# Revit family: VIESSMANN - Vitocell 100-V (CVW.CVWA) 390-500 L
name_source: partatom
category: Wyposażenie mechaniczne
revit_build: Autodesk Revit 2017 (Build: 20160720_1515(x64)
units: mm (PartAtom-declared; Revit-internal decimal feet)

## family parameters
Numer OmniClass = 23.65.35.11.11
Oparty na płaszczyźnie roboczej = Nie
Punkt obliczania pomieszczeń = Nie
Tnij formami wycięć po wczytaniu = Tak
Typ części = Normalny
Tytuł OmniClass = Storage Water Heaters
Współdzielony = Nie
Wymiar okrągłego złącza = Użyj średnicy
Zawsze pionowo = Tak

## types (2) — shared parameters
Autor = https://www.archispace.pl
Ciepła woda użytkowa = 1"
Cyrkulacja = 3/4"
Grzałka elektryczna = 1 1/2"
Klasa efektywności energetycznej = B
Maks. powierzchnia czynna absorbera możliwa do podłączenia do zestawu solarnych wymienników ciepła - Vitosol-F = 11.5 m²
Maks. powierzchnia czynna absorbera możliwa do podłączenia do zestawu solarnych wymienników ciepła - Vitosol-T = 6.0 m²
Numer identyfikacyjny produktu = 9W173-13MC/E
Opis = Podgrzewacz pojemnościowy
Opis indeksowy = 9W173-13MC/E
Podział = 859 mm  [stored 2.81824 ft]
Powrót wody grzewczej = 1 1/4"
Producent = Viessmann Sp.z.o.o.
Przepływ objętościowy wody grzewczej (dla podanych wydajności stałych) = 3.00 m³/h
Przepływ po stronie wody grzewczej = 3.00 m³/h
Szerokość - bez izolacji cieplnej = 881 mm  [stored 2.89042 ft]
Szerokość - z izolacją cieplną = 923 mm  [stored 3.02822 ft]
Szerokość z izolacją cieplną = 923 mm  [stored 3.02822 ft]
URL = https://www.viessmann-projektant.pl
Viessmann Kolor 1 = Viessmann Kolor 1
Viessmann Kolor 2 = Viessmann Kolor 2
Viessmann Kolor 3 = Viessmann Kolor 3
Wysokość króćca cwu z zestawu solarnych wymienników ciepła = 572 mm  [stored 1.87664 ft]
Wysokość króćca powrotu wody grzewczej = 330 mm  [stored 1.08268 ft]
Wysokość króćca zimnej wody użytkowej = 88 mm  [stored 0.288714 ft]
Zasilanie wody grzewczej = 1 1/4"
Zestaw solarnych wymienników ciepła = 3/4"
Zimna woda użytkowa = 1"
Średnica - bez izolacji cieplnej = 650 mm  [stored 2.13255 ft]
Średnica - z izolacją cieplną = 859 mm  [stored 2.81824 ft]
Średnica z izolacją cieplną = 859 mm  [stored 2.81824 ft]

## per-type parameters (varying)
- Zbiornik CVWA 500L: Czas podgrzewu cwu przy podłączonej pompie ciepła o znamionowej mocy cieplnej 16kW i temp. wody na zasilaniu wodą grzewczą wynoszącej 55 lub 65°C - przy podgrzewie cwu z 10 do 45°C=66 min; Czas podgrzewu cwu przy podłączonej pompie ciepła o znamionowej mocy cieplnej 16kW i temp. wody na zasilaniu wodą grzewczą wynoszącej 55 lub 65°C - przy podgrzewie cwu z 10 do 55°C=85 min; Ilość ciepła dyżurnego=1.90 kWh/24h; Maks. ilość pobierana przy temperaturze na zasilaniu wodą grzewczą 70℃=59; Maks. ilość pobierana przy temperaturze na zasilaniu wodą grzewczą 80℃=66; Maks. ilość pobierana przy temperaturze na zasilaniu wodą grzewczą 90℃=69; Maks. możliwa do przyłączenia moc pompy ciepła przy temp. wody na zasilaniu wodą grzewczą wynoszącej 65°C, temp. cwu 55°C oraz podanym przepływie objętościowym wody grzewczej=17000 W; Masa całkowita z izolacją cieplną=200.00 kg; Model=Podgrzewacz pojemnościowy Viessmann Vitocell 100-V CVWA 500L / Hot water storage tank Viessmann Vitocell 100-V CVWA 500L; Objętość brutto=540.0 L; Objętość wody grzewczej=40.0 L; Opory przepływu po stronie wody grzewczej=7500.0 Pa; Opory przepływu po stronie wody użytkowej=6500.0 Pa; Pobierana ilość cwu bez dogrzewu - zawartość podgrzewacza podgrzana o 45°C=350.0 L; Pobierana ilość cwu bez dogrzewu - zawartość podgrzewacza podgrzana o 55°C=350.0 L; Pojemność podgrzewacza=500.0 L; Powierzchnia grzewcza=5.5 m²; Przepływ objętościowy wody grzewczej (przy podgrzewie cwu z 10 na 45℃) przy temperaturze na zasilaniu wodą grzewczą 50℃=0.88; Przepływ objętościowy wody grzewczej (przy podgrzewie cwu z 10 na 45℃) przy temperaturze na zasilaniu wodą grzewczą 60℃=1.45; Przepływ objętościowy wody grzewczej (przy podgrzewie cwu z 10 na 45℃) przy temperaturze na zasilaniu wodą grzewczą 70℃=1.95; Przepływ objętościowy wody grzewczej (przy podgrzewie cwu z 10 na 45℃) przy temperaturze na zasilaniu wodą grzewczą 80℃=2.43; Przepływ objętościowy wody grzewczej (przy podgrzewie cwu z 10 na 45℃) przy temperaturze na zasilaniu wodą grzewczą 90℃=2.90; Przepływ objętościowy wody grzewczej (przy podgrzewie cwu z 10 na 60℃) przy temperaturze na zasilaniu wodą grzewczą 70℃=1.01; Przepływ objętościowy wody grzewczej (przy podgrzewie cwu z 10 na 60℃) przy temperaturze na zasilaniu wodą grzewczą 80℃=1.40; Przepływ objętościowy wody grzewczej (przy podgrzewie cwu z 10 na 60℃) przy temperaturze na zasilaniu wodą grzewczą 90℃=1.75; Przepływ po stronie wody użytkowej=2.90 m³/h; Wsp. mocy NL w połączeniu z pompą ciepła - temp. na ładowaniu podgrzewacza cwu 45℃=3.5; Wsp. mocy NL w połączeniu z pompą ciepła - temp. na ładowaniu podgrzewacza cwu 50℃=3.9; Współczynnik mocy NL przy temperaturze na zasilaniu wodą grzewczą 70℃=13.3; Współczynnik mocy NL przy temperaturze na zasilaniu wodą grzewczą 80℃=14.9; Współczynnik mocy NL przy temperaturze na zasilaniu wodą grzewczą 90℃=16.5; Wydajność krótkotrwała przy temperaturze na zasilaniu wodą grzewczą 70℃=596 L/10min; Wydajność krótkotrwała przy temperaturze na zasilaniu wodą grzewczą 80℃=667 L/10min; Wydajność krótkotrwała przy temperaturze na zasilaniu wodą grzewczą 90℃=690 L/10min; Wydajność stała (przy podgrzewie cwu z 10 na 45℃ i temperaturze na zasilaniu wodą grzewczą 50℃=36000; Wydajność stała (przy podgrzewie cwu z 10 na 45℃ i temperaturze na zasilaniu wodą grzewczą 60℃=59000; Wydajność stała (przy podgrzewie cwu z 10 na 45℃ i temperaturze na zasilaniu wodą grzewczą 70℃=79000; Wydajność stała (przy podgrzewie cwu z 10 na 45℃ i temperaturze na zasilaniu wodą grzewczą 80℃=99000; Wydajność stała (przy podgrzewie cwu z 10 na 45℃ i temperaturze na zasilaniu wodą grzewczą 90℃=118000; Wydajność stała (przy podgrzewie cwu z 10 na 60℃ i temperaturze na zasilaniu wodą grzewczą 70℃=59000; Wydajność stała (przy podgrzewie cwu z 10 na 60℃ i temperaturze na zasilaniu wodą grzewczą 80℃=81000; Wydajność stała (przy podgrzewie cwu z 10 na 60℃ i temperaturze na zasilaniu wodą grzewczą 90℃=102000; Wymiar przechylenia - bez izolacji cieplnej=1860 mm  [stored 6.10236 ft]; Wysokość - bez izolacji cieplnej=1844 mm  [stored 6.04987 ft]; Wysokość - z izolacją cieplną=1948 mm  [stored 6.39108 ft]; Wysokość i izolacją cieplną=1948 mm  [stored 6.39108 ft]; Wysokość króćca cwu=1765 mm  [stored 5.79068 ft]; Wysokość króćca cyrkulacji=1370 mm; Wysokość króćca zasilania wodą grzewczą=1250 mm  [stored 4.10105 ft]
- Zbiornik CVWA 390L: Czas podgrzewu cwu przy podłączonej pompie ciepła o znamionowej mocy cieplnej 16kW i temp. wody na zasilaniu wodą grzewczą wynoszącej 55 lub 65°C - przy podgrzewie cwu z 10 do 45°C=60 min; Czas podgrzewu cwu przy podłączonej pompie ciepła o znamionowej mocy cieplnej 16kW i temp. wody na zasilaniu wodą grzewczą wynoszącej 55 lub 65°C - przy podgrzewie cwu z 10 do 55°C=76 min; Ilość ciepła dyżurnego=1.80 kWh/24h; Maks. ilość pobierana przy temperaturze na zasilaniu wodą grzewczą 70℃=46; Maks. ilość pobierana przy temperaturze na zasilaniu wodą grzewczą 80℃=52; Maks. ilość pobierana przy temperaturze na zasilaniu wodą grzewczą 90℃=54; Maks. możliwa do przyłączenia moc pompy ciepła przy temp. wody na zasilaniu wodą grzewczą wynoszącej 65°C, temp. cwu 55°C oraz podanym przepływie objętościowym wody grzewczej=15000 W; Masa całkowita z izolacją cieplną=190.00 kg; Model=Podgrzewacz pojemnościowy Viessmann Vitocell 100-V CVWA 390L / Hot water storage tank Viessmann Vitocell 100-V CVWA 390L; Objętość brutto=417.0 L; Objętość wody grzewczej=27.0 L; Opory przepływu po stronie wody grzewczej=3500.0 Pa; Opory przepływu po stronie wody użytkowej=300.0 Pa; Pobierana ilość cwu bez dogrzewu - zawartość podgrzewacza podgrzana o 45°C=285.0 L; Pobierana ilość cwu bez dogrzewu - zawartość podgrzewacza podgrzana o 55°C=285.0 L; Pojemność podgrzewacza=390.0 L; Powierzchnia grzewcza=4.0 m²; Przepływ objętościowy wody grzewczej (przy podgrzewie cwu z 10 na 45℃) przy temperaturze na zasilaniu wodą grzewczą 50℃=0.72; Przepływ objętościowy wody grzewczej (przy podgrzewie cwu z 10 na 45℃) przy temperaturze na zasilaniu wodą grzewczą 60℃=1.20; Przepływ objętościowy wody grzewczej (przy podgrzewie cwu z 10 na 45℃) przy temperaturze na zasilaniu wodą grzewczą 70℃=1.62; Przepływ objętościowy wody grzewczej (przy podgrzewie cwu z 10 na 45℃) przy temperaturze na zasilaniu wodą grzewczą 80℃=2.03; Przepływ objętościowy wody grzewczej (przy podgrzewie cwu z 10 na 45℃) przy temperaturze na zasilaniu wodą grzewczą 90℃=2.42; Przepływ objętościowy wody grzewczej (przy podgrzewie cwu z 10 na 60℃) przy temperaturze na zasilaniu wodą grzewczą 70℃=0.83; Przepływ objętościowy wody grzewczej (przy podgrzewie cwu z 10 na 60℃) przy temperaturze na zasilaniu wodą grzewczą 80℃=1.16; Przepływ objętościowy wody grzewczej (przy podgrzewie cwu z 10 na 60℃) przy temperaturze na zasilaniu wodą grzewczą 90℃=1.46; Przepływ po stronie wody użytkowej=2.42 m³/h; Wsp. mocy NL w połączeniu z pompą ciepła - temp. na ładowaniu podgrzewacza cwu 45℃=2.5; Wsp. mocy NL w połączeniu z pompą ciepła - temp. na ładowaniu podgrzewacza cwu 50℃=2.8; Współczynnik mocy NL przy temperaturze na zasilaniu wodą grzewczą 70℃=10; Współczynnik mocy NL przy temperaturze na zasilaniu wodą grzewczą 80℃=11.3; Współczynnik mocy NL przy temperaturze na zasilaniu wodą grzewczą 90℃=12.6; Wydajność krótkotrwała przy temperaturze na zasilaniu wodą grzewczą 70℃=455 L/10min; Wydajność krótkotrwała przy temperaturze na zasilaniu wodą grzewczą 80℃=521 L/10min; Wydajność krótkotrwała przy temperaturze na zasilaniu wodą grzewczą 90℃=540 L/10min; Wydajność stała (przy podgrzewie cwu z 10 na 45℃ i temperaturze na zasilaniu wodą grzewczą 50℃=29000; Wydajność stała (przy podgrzewie cwu z 10 na 45℃ i temperaturze na zasilaniu wodą grzewczą 60℃=49000; Wydajność stała (przy podgrzewie cwu z 10 na 45℃ i temperaturze na zasilaniu wodą grzewczą 70℃=66000; Wydajność stała (przy podgrzewie cwu z 10 na 45℃ i temperaturze na zasilaniu wodą grzewczą 80℃=82000; Wydajność stała (przy podgrzewie cwu z 10 na 45℃ i temperaturze na zasilaniu wodą grzewczą 90℃=98000; Wydajność stała (przy podgrzewie cwu z 10 na 60℃ i temperaturze na zasilaniu wodą grzewczą 70℃=48000; Wydajność stała (przy podgrzewie cwu z 10 na 60℃ i temperaturze na zasilaniu wodą grzewczą 80℃=67000; Wydajność stała (przy podgrzewie cwu z 10 na 60℃ i temperaturze na zasilaniu wodą grzewczą 90℃=85000; Wymiar przechylenia - bez izolacji cieplnej=1550 mm  [stored 5.0853 ft]; Wysokość - bez izolacji cieplnej=1522 mm  [stored 4.99344 ft]; Wysokość - z izolacją cieplną=1624 mm  [stored 5.32808 ft]; Wysokość i izolacją cieplną=1624 mm  [stored 5.32808 ft]; Wysokość króćca cwu=1439 mm; Wysokość króćca cyrkulacji=1070 mm  [stored 3.5105 ft]; Wysokość króćca zasilania wodą grzewczą=950 mm  [stored 3.1168 ft]

note: source unit labels omitted for Maks. ilość pobierana przy temperaturze na zasilaniu wodą grzewczą 70℃, Maks. ilość pobierana przy temperaturze na zasilaniu wodą grzewczą 80℃, Maks. ilość pobierana przy temperaturze na zasilaniu wodą grzewczą 90℃, Przepływ objętościowy wody grzewczej (przy podgrzewie cwu z 10 na 45℃) przy temperaturze na zasilaniu wodą grzewczą 50℃, Przepływ objętościowy wody grzewczej (przy podgrzewie cwu z 10 na 45℃) przy temperaturze na zasilaniu wodą grzewczą 60℃, Przepływ objętościowy wody grzewczej (przy podgrzewie cwu z 10 na 45℃) przy temperaturze na zasilaniu wodą grzewczą 70℃, Przepływ objętościowy wody grzewczej (przy podgrzewie cwu z 10 na 45℃) przy temperaturze na zasilaniu wodą grzewczą 80℃, Przepływ objętościowy wody grzewczej (przy podgrzewie cwu z 10 na 45℃) przy temperaturze na zasilaniu wodą grzewczą 90℃, Przepływ objętościowy wody grzewczej (przy podgrzewie cwu z 10 na 60℃) przy temperaturze na zasilaniu wodą grzewczą 70℃, Przepływ objętościowy wody grzewczej (przy podgrzewie cwu z 10 na 60℃) przy temperaturze na zasilaniu wodą grzewczą 80℃, Przepływ objętościowy wody grzewczej (przy podgrzewie cwu z 10 na 60℃) przy temperaturze na zasilaniu wodą grzewczą 90℃, Wydajność stała (przy podgrzewie cwu z 10 na 45℃ i temperaturze na zasilaniu wodą grzewczą 50℃, Wydajność stała (przy podgrzewie cwu z 10 na 45℃ i temperaturze na zasilaniu wodą grzewczą 60℃, Wydajność stała (przy podgrzewie cwu z 10 na 45℃ i temperaturze na zasilaniu wodą grzewczą 70℃, Wydajność stała (przy podgrzewie cwu z 10 na 45℃ i temperaturze na zasilaniu wodą grzewczą 80℃, Wydajność stała (przy podgrzewie cwu z 10 na 45℃ i temperaturze na zasilaniu wodą grzewczą 90℃, Wydajność stała (przy podgrzewie cwu z 10 na 60℃ i temperaturze na zasilaniu wodą grzewczą 70℃, Wydajność stała (przy podgrzewie cwu z 10 na 60℃ i temperaturze na zasilaniu wodą grzewczą 80℃, Wydajność stała (przy podgrzewie cwu z 10 na 60℃ i temperaturze na zasilaniu wodą grzewczą 90℃ — the stored unit's dimension contradicts the parameter name (converter mislabeling)

note: [stored X ft] marks values corroborated as IEEE doubles in the binary element streams (Revit-internal decimal feet)
